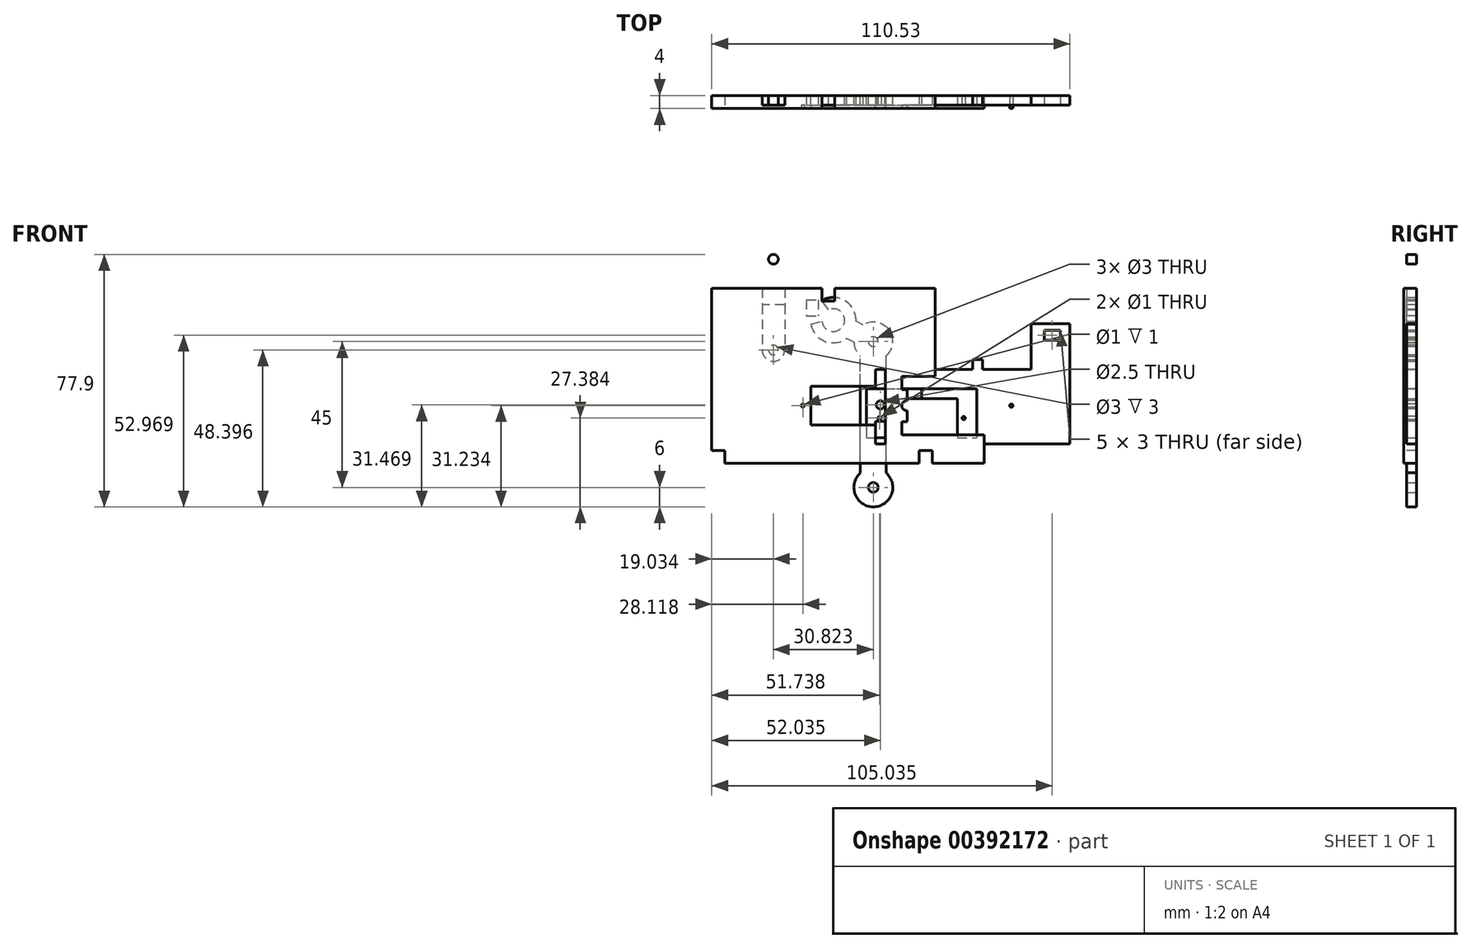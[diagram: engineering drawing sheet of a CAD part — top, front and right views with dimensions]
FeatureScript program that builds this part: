
annotation { "Feature Type Name" : "Feature", "Feature Type Description" : "" }
export const myFeature = defineFeature(function(context is Context, id is Id, definition is map)
    precondition{}
    {
        {
            var Q0;
            Q0=qCreatedBy(makeId("Front.planeOp"),FACE);
            var sketch = newSketch(context, id + "F0", { "sketchPlane" : qUnion([Q0])});
            skLineSegment(sketch, "E0.bottom", {"start": v(-55.1, 26.52) * mm, "end": v(28.9, 26.52) * mm});
            skLineSegment(sketch, "E0.top", {"start": v(-55.1, -27.48) * mm, "end": v(28.9, -27.48) * mm});
            skLineSegment(sketch, "E0.left", {"start": v(-55.1, 26.52) * mm, "end": v(-55.1, -27.48) * mm});
            skLineSegment(sketch, "E0.right", {"start": v(28.9, 26.52) * mm, "end": v(28.9, -27.48) * mm});
            skSolve(sketch);
        }
        {
            var Q0;
            Q0=makeQuery(id+"F0.imprint","IMPRINT",FACE,{"disambiguationData":[TD([[makeQuery(id+"F0.imprint","IMPRINT",EDGE,{"derivedFrom":sQuery(id+"F0.wireOp",EDGE,"E0.bottom")}),-1.0]])]});
            var sketch = newSketch(context, id + "F1", { "sketchPlane" : qUnion([Q0])});
            skSolve(sketch);
        }
        {
            var Q0;
            Q0 = qSketchRegion(id + "F1", true);
            var Q1;
            Q1=makeQuery(id+"F0.imprint","IMPRINT",FACE,{"disambiguationData":[TD([[makeQuery(id+"F0.imprint","IMPRINT",EDGE,{"derivedFrom":sQuery(id+"F0.wireOp",EDGE,"E0.bottom")}),-1.0]])]});
            extrude(context, id + "F2", {"entities" : qUnion([Q0, Q1]), "depth" : 4 * mm});
        }
        {
            var Q0;
            Q0=makeQuery(id+"F2.opExtrude","CAP_FACE",FACE,{"disambiguationData":[OSD([sQuery(id+"F0.wireOp",EDGE,"E0.bottom"),sQuery(id+"F0.wireOp",EDGE,"E0.top"),sQuery(id+"F0.wireOp",EDGE,"E0.left"),sQuery(id+"F0.wireOp",EDGE,"E0.right")])],"isStart":false});
            var sketch = newSketch(context, id + "F3", { "sketchPlane" : qUnion([Q0])});
            skLineSegment(sketch, "E1.bottom", {"start": v(28.9, 26.52) * mm, "end": v(13.9, 26.52) * mm});
            skLineSegment(sketch, "E1.top", {"start": v(28.9, -7.48) * mm, "end": v(13.9, -7.48) * mm});
            skLineSegment(sketch, "E1.left", {"start": v(28.9, 26.52) * mm, "end": v(28.9, -7.48) * mm});
            skLineSegment(sketch, "E1.right", {"start": v(13.9, 26.52) * mm, "end": v(13.9, -7.48) * mm});
            skSolve(sketch);
        }
        {
            var Q0;
            Q0=makeQuery(id+"F3.imprint","IMPRINT",FACE,{"disambiguationData":[TD([[makeQuery(id+"F3.imprint","IMPRINT",EDGE,{"derivedFrom":sQuery(id+"F3.wireOp",EDGE,"E1.bottom")}),-1.0]])]});
            extrude(context, id + "F4", {"entities" : qUnion([Q0]), "operationType" : NewBodyOperationType.REMOVE, "oppositeDirection" : true, "depth" : 5 * mm});
        }
        {
            var Q0;
            Q0=makeQuery(id+"F2.opExtrude","CAP_FACE",FACE,{"disambiguationData":[OSD([sQuery(id+"F0.wireOp",EDGE,"E0.bottom"),sQuery(id+"F0.wireOp",EDGE,"E0.top"),sQuery(id+"F0.wireOp",EDGE,"E0.left"),sQuery(id+"F0.wireOp",EDGE,"E0.right")])],"isStart":false});
            var sketch = newSketch(context, id + "F5", { "sketchPlane" : qUnion([Q0])});
            skLineSegment(sketch, "E2", {"start": v(28.9, -27.48) * mm, "end": v(12.9, -27.48) * mm});
            skLineSegment(sketch, "E3.bottom", {"start": v(12.9, -27.48) * mm, "end": v(8.9, -27.48) * mm});
            skLineSegment(sketch, "E3.top", {"start": v(12.9, -23.48) * mm, "end": v(8.9, -23.48) * mm});
            skLineSegment(sketch, "E3.left", {"start": v(12.9, -27.48) * mm, "end": v(12.9, -23.48) * mm});
            skLineSegment(sketch, "E3.right", {"start": v(8.9, -27.48) * mm, "end": v(8.9, -23.48) * mm});
            skLineSegment(sketch, "E4.bottom", {"start": v(-55.1, -27.48) * mm, "end": v(-51.1, -27.48) * mm});
            skLineSegment(sketch, "E4.top", {"start": v(-55.1, -23.48) * mm, "end": v(-51.1, -23.48) * mm});
            skLineSegment(sketch, "E4.left", {"start": v(-55.1, -27.48) * mm, "end": v(-55.1, -23.48) * mm});
            skLineSegment(sketch, "E4.right", {"start": v(-51.1, -27.48) * mm, "end": v(-51.1, -23.48) * mm});
            skLineSegment(sketch, "E5", {"start": v(13.9, 26.52) * mm, "end": v(-17.1, 26.52) * mm});
            skLineSegment(sketch, "E6.bottom", {"start": v(-17.1, 26.52) * mm, "end": v(-21.1, 26.52) * mm});
            skLineSegment(sketch, "E6.top", {"start": v(-17.1, 22.52) * mm, "end": v(-21.1, 22.52) * mm});
            skLineSegment(sketch, "E6.left", {"start": v(-17.1, 26.52) * mm, "end": v(-17.1, 22.52) * mm});
            skLineSegment(sketch, "E6.right", {"start": v(-21.1, 26.52) * mm, "end": v(-21.1, 22.52) * mm});
            skSolve(sketch);
        }
        {
            var Q0;
            Q0=makeQuery(id+"F5.imprint","IMPRINT",FACE,{"disambiguationData":[TD([[makeQuery(id+"F5.imprint","IMPRINT",EDGE,{"derivedFrom":sQuery(id+"F5.wireOp",EDGE,"E6.bottom")}),-1.0]])]});
            var Q1;
            Q1=makeQuery(id+"F5.imprint","IMPRINT",FACE,{"disambiguationData":[TD([[makeQuery(id+"F5.imprint","IMPRINT",EDGE,{"derivedFrom":sQuery(id+"F5.wireOp",EDGE,"E4.bottom")}),1.0]])]});
            var Q2;
            Q2=makeQuery(id+"F5.imprint","IMPRINT",FACE,{"disambiguationData":[TD([[makeQuery(id+"F5.imprint","IMPRINT",EDGE,{"derivedFrom":sQuery(id+"F5.wireOp",EDGE,"E3.bottom")}),1.0]])]});
            extrude(context, id + "F6", {"entities" : qUnion([Q0, Q1, Q2]), "operationType" : NewBodyOperationType.REMOVE, "oppositeDirection" : true, "depth" : 5 * mm});
        }
        {
            var Q0;
            Q0=qCreatedBy(makeId("Front.planeOp"),FACE);
            var sketch = newSketch(context, id + "F7", { "sketchPlane" : qUnion([Q0])});
            skLineSegment(sketch, "E7.bottom", {"start": v(-30.5, -0.7) * mm, "end": v(40.5, -0.7) * mm});
            skLineSegment(sketch, "E7.top", {"start": v(-30.5, -18.7) * mm, "end": v(40.5, -18.7) * mm});
            skLineSegment(sketch, "E7.left", {"start": v(-30.5, -0.7) * mm, "end": v(-30.5, -18.7) * mm});
            skLineSegment(sketch, "E7.right", {"start": v(40.5, -0.7) * mm, "end": v(40.5, -18.7) * mm});
            skSolve(sketch);
        }
        {
            var Q0;
            Q0=makeQuery(id+"F7.imprint","IMPRINT",FACE,{"disambiguationData":[TD([[makeQuery(id+"F7.imprint","IMPRINT",EDGE,{"derivedFrom":sQuery(id+"F7.wireOp",EDGE,"E7.bottom")}),-1.0]])]});
            extrude(context, id + "F8", {"entities" : qUnion([Q0]), "depth" : 4 * mm});
        }
        {
            var Q0;
            Q0=makeQuery(id+"F8.opExtrude","CAP_FACE",FACE,{"disambiguationData":[OSD([sQuery(id+"F7.wireOp",EDGE,"E7.bottom"),sQuery(id+"F7.wireOp",EDGE,"E7.top"),sQuery(id+"F7.wireOp",EDGE,"E7.left"),sQuery(id+"F7.wireOp",EDGE,"E7.right")])],"isStart":false});
            var sketch = newSketch(context, id + "F9", { "sketchPlane" : qUnion([Q0])});
            skLineSegment(sketch, "E8", {"start": v(-30.5, -9.7) * mm, "end": v(-24.5, -9.7) * mm});
            skLineSegment(sketch, "E9", {"start": v(-15.75, -0.7) * mm, "end": v(-15.75, -3.7) * mm});
            skLineSegment(sketch, "E10", {"start": v(-15.75, -3.7) * mm, "end": v(-24.5, -3.7) * mm});
            skLineSegment(sketch, "E11", {"start": v(-24.5, -3.7) * mm, "end": v(-24.5, -18.7) * mm});
            skLineSegment(sketch, "E12.bottom", {"start": v(-24.5, -3.7) * mm, "end": v(-1.5, -3.7) * mm});
            skLineSegment(sketch, "E12.top", {"start": v(-24.5, -15.7) * mm, "end": v(-1.5, -15.7) * mm});
            skLineSegment(sketch, "E12.left", {"start": v(-24.5, -3.7) * mm, "end": v(-24.5, -15.7) * mm});
            skLineSegment(sketch, "E12.right", {"start": v(-1.5, -3.7) * mm, "end": v(-1.5, -15.7) * mm});
            skLineSegment(sketch, "E13", {"start": v(40.5, -9.7) * mm, "end": v(34.5, -9.7) * mm});
            skPoint(sketch, "E13.endSnap0", {"position": v(40.5, -9.7) * mm});
            skLineSegment(sketch, "E14", {"start": v(34.5, -9.7) * mm, "end": v(34.5, 8.83) * mm});
            skLineSegment(sketch, "E15", {"start": v(27.7, -0.7) * mm, "end": v(27.7, -3.7) * mm});
            skLineSegment(sketch, "E16", {"start": v(27.7, -3.7) * mm, "end": v(34.5, -3.7) * mm});
            skLineSegment(sketch, "E17.bottom", {"start": v(34.5, -3.7) * mm, "end": v(11.5, -3.7) * mm});
            skLineSegment(sketch, "E17.top", {"start": v(34.5, -15.7) * mm, "end": v(11.5, -15.7) * mm});
            skLineSegment(sketch, "E17.left", {"start": v(34.5, -3.7) * mm, "end": v(34.5, -15.7) * mm});
            skLineSegment(sketch, "E17.right", {"start": v(11.5, -3.7) * mm, "end": v(11.5, -15.7) * mm});
            skSolve(sketch);
        }
        {
            var Q0;
            {var subQ4=sQuery(id+"F9.wireOp",EDGE,"E12.top");Q0=makeQuery(id+"F9.imprint","IMPRINT",FACE,{"disambiguationData":[TD([[makeQuery(id+"F9.imprint","IMPRINT",EDGE,{"derivedFrom":subQ4}),1.0]])]});}
            var Q1;
            {var subQ4=sQuery(id+"F9.wireOp",EDGE,"E17.top");Q1=makeQuery(id+"F9.imprint","IMPRINT",FACE,{"disambiguationData":[TD([[makeQuery(id+"F9.imprint","IMPRINT",EDGE,{"derivedFrom":subQ4}),-1.0]])]});}
            extrude(context, id + "F10", {"entities" : qUnion([Q0, Q1]), "operationType" : NewBodyOperationType.REMOVE, "oppositeDirection" : true, "depth" : 5 * mm});
        }
        {
            var Q0;
            Q0=makeQuery(id+"F8.opExtrude","CAP_FACE",FACE,{"disambiguationData":[OSD([sQuery(id+"F7.wireOp",EDGE,"E7.bottom"),sQuery(id+"F7.wireOp",EDGE,"E7.top"),sQuery(id+"F7.wireOp",EDGE,"E7.left"),sQuery(id+"F7.wireOp",EDGE,"E7.right")])],"isStart":false});
            var sketch = newSketch(context, id + "F11", { "sketchPlane" : qUnion([Q0])});
            skLineSegment(sketch, "E18", {"start": v(11.5, -3.7) * mm, "end": v(6.5, -3.7) * mm});
            skPoint(sketch, "E18.endSnap0", {"position": v(5, -0.7) * mm});
            skLineSegment(sketch, "E19", {"start": v(-1.5, -3.7) * mm, "end": v(3.5, -3.7) * mm});
            skLineSegment(sketch, "E20", {"start": v(3.5, -3.7) * mm, "end": v(3.5, 4.46) * mm});
            skPoint(sketch, "E21.firstSnap0", {"position": v(3.5, 0.38) * mm});
            skLineSegment(sketch, "E21.bottom", {"start": v(3.5, -0.7) * mm, "end": v(6.5, -0.7) * mm});
            skLineSegment(sketch, "E21.top", {"start": v(3.5, -4.7) * mm, "end": v(6.5, -4.7) * mm});
            skLineSegment(sketch, "E21.left", {"start": v(3.5, -0.7) * mm, "end": v(3.5, -4.7) * mm});
            skLineSegment(sketch, "E21.right", {"start": v(6.5, -0.7) * mm, "end": v(6.5, -4.7) * mm});
            skLineSegment(sketch, "E22", {"start": v(-7.33, -9.7) * mm, "end": v(23.66, -9.7) * mm});
            skPoint(sketch, "E22.startSnap0", {"position": v(-1.5, -9.7) * mm});
            skLineSegment(sketch, "E23.MirrorCS", {"start": v(3.5, -14.7) * mm, "end": v(6.5, -14.7) * mm});
            skLineSegment(sketch, "E24.MirrorCS", {"start": v(6.5, -18.7) * mm, "end": v(6.5, -14.7) * mm});
            skLineSegment(sketch, "E25.MirrorCS", {"start": v(3.5, -15.7) * mm, "end": v(3.5, -23.85) * mm});
            skLineSegment(sketch, "E26.MirrorCS", {"start": v(3.5, -18.7) * mm, "end": v(3.5, -14.7) * mm});
            skLineSegment(sketch, "E27.MirrorCS", {"start": v(3.5, -18.7) * mm, "end": v(6.5, -18.7) * mm});
            skLineSegment(sketch, "E28.MirrorCS", {"start": v(-1.5, -15.7) * mm, "end": v(3.5, -15.7) * mm});
            skLineSegment(sketch, "E29.MirrorCS", {"start": v(11.5, -15.7) * mm, "end": v(6.5, -15.7) * mm});
            skSolve(sketch);
        }
        {
            var Q0;
            {var subQ3=sQuery(id+"F11.wireOp",EDGE,"E21.bottom");Q0=makeQuery(id+"F11.imprint","IMPRINT",FACE,{"disambiguationData":[TD([[makeQuery(id+"F11.imprint","IMPRINT",EDGE,{"derivedFrom":subQ3}),-1.0]])]});}
            var Q1;
            {var subQ5=sQuery(id+"F11.wireOp",EDGE,"E23.MirrorCS");Q1=makeQuery(id+"F11.imprint","IMPRINT",FACE,{"disambiguationData":[TD([[makeQuery(id+"F11.imprint","IMPRINT",EDGE,{"derivedFrom":subQ5}),-1.0]])]});}
            extrude(context, id + "F12", {"entities" : qUnion([Q0, Q1]), "operationType" : NewBodyOperationType.REMOVE, "oppositeDirection" : true, "depth" : 5 * mm});
        }
        {
            var Q0;
            Q0=makeQuery(id+"F8.opExtrude","CAP_FACE",FACE,{"disambiguationData":[OSD([sQuery(id+"F7.wireOp",EDGE,"E7.bottom"),sQuery(id+"F7.wireOp",EDGE,"E7.top"),sQuery(id+"F7.wireOp",EDGE,"E7.left"),sQuery(id+"F7.wireOp",EDGE,"E7.right")])],"isStart":false});
            var sketch = newSketch(context, id + "F13", { "sketchPlane" : qUnion([Q0])});
            skLineSegment(sketch, "E30", {"start": v(-30.5, -9.7) * mm, "end": v(-27, -9.7) * mm});
            skPoint(sketch, "E30.endSnap0", {"position": v(-24.5, -9.7) * mm});
            skCircle(sketch, "E31", {"center": v(-27, -9.7) * mm, "radius": 0.5 * mm});
            skLineSegment(sketch, "E32", {"start": v(5.16, 3.88) * mm, "end": v(5.16, -32.27) * mm});
            skLineSegment(sketch, "E33.MirrorCS", {"start": v(40.8, -9.7) * mm, "end": v(37.3, -9.7) * mm});
            skCircle(sketch, "E34.MirrorC", {"center": v(37.3, -9.7) * mm, "radius": 0.5 * mm});
            skSolve(sketch);
        }
        {
            var Q0;
            Q0=makeQuery(id+"F13.imprint","IMPRINT",FACE,{"disambiguationData":[TD([[makeQuery(id+"F13.imprint","IMPRINT",EDGE,{"derivedFrom":sQuery(id+"F13.wireOp",EDGE,"E31")}),1.0]])]});
            var Q1;
            Q1=makeQuery(id+"F13.imprint","IMPRINT",FACE,{"disambiguationData":[TD([[makeQuery(id+"F13.imprint","IMPRINT",EDGE,{"derivedFrom":sQuery(id+"F13.wireOp",EDGE,"E34.MirrorC")}),-1.0]])]});
            extrude(context, id + "F14", {"entities" : qUnion([Q0, Q1]), "operationType" : NewBodyOperationType.REMOVE, "oppositeDirection" : true, "depth" : 5 * mm});
        }
        {
            var Q0;
            Q0=makeQuery(id+"F8.opExtrude","CAP_FACE",FACE,{"disambiguationData":[OSD([sQuery(id+"F7.wireOp",EDGE,"E7.bottom"),sQuery(id+"F7.wireOp",EDGE,"E7.top"),sQuery(id+"F7.wireOp",EDGE,"E7.left"),sQuery(id+"F7.wireOp",EDGE,"E7.right")])],"isStart":false});
            var sketch = newSketch(context, id + "F15", { "sketchPlane" : qUnion([Q0])});
            skLineSegment(sketch, "E35", {"start": v(5, -4.7) * mm, "end": v(5, -9.7) * mm});
            skPoint(sketch, "E35.endSnap0", {"position": v(5, -14.7) * mm});
            skCircle(sketch, "E36", {"center": v(5, -9.7) * mm, "radius": 1.5 * mm});
            skLineSegment(sketch, "E37", {"start": v(11.5, -9.7) * mm, "end": v(9.5, -9.7) * mm});
            skCircle(sketch, "E38", {"center": v(9.5, -9.7) * mm, "radius": 0.5 * mm});
            skLineSegment(sketch, "E39", {"start": v(5.2, -0.7) * mm, "end": v(5.2, -24.79) * mm});
            skCircle(sketch, "E40.MirrorC", {"center": v(0.9, -9.7) * mm, "radius": 0.5 * mm});
            skLineSegment(sketch, "E41.MirrorCS", {"start": v(-1.1, -9.7) * mm, "end": v(0.9, -9.7) * mm});
            skSolve(sketch);
        }
        {
            var Q0;
            Q0=makeQuery(id+"F15.imprint","IMPRINT",FACE,{"disambiguationData":[TD([[makeQuery(id+"F15.imprint","IMPRINT",EDGE,{"derivedFrom":sQuery(id+"F15.wireOp",EDGE,"E40.MirrorC")}),-1.0]])]});
            var Q1;
            Q1=makeQuery(id+"F15.imprint","IMPRINT",FACE,{"disambiguationData":[TD([[makeQuery(id+"F15.imprint","IMPRINT",EDGE,{"derivedFrom":sQuery(id+"F15.wireOp",EDGE,"E38")}),1.0]])]});
            var Q2;
            {var subQ0=sQuery(id+"F15.wireOp",EDGE,"E36");var subQ1=makeQuery(id+"F15.imprint","INTERSECT",VERTEX,{"derivedFrom":[sQuery(id+"F15.wireOp",EDGE,"E35"),subQ0]});Q2=makeQuery(id+"F15.imprint","IMPRINT",FACE,{"disambiguationData":[TD([[makeQuery(id+"F15.imprint","IMPRINT",EDGE,{"disambiguationData":[TD([[subQ1,1.0]])],"derivedFrom":subQ0}),1.0]])]});}
            var Q3;
            {var subQ0=sQuery(id+"F15.wireOp",EDGE,"E39");var subQ1=sQuery(id+"F15.wireOp",EDGE,"E36");var subQ2=makeQuery(id+"F15.imprint","INTERSECT",VERTEX,{"disambiguationData":[OD(0.0)],"derivedFrom":[subQ1,subQ0]});Q3=makeQuery(id+"F15.imprint","IMPRINT",FACE,{"disambiguationData":[TD([[makeQuery(id+"F15.imprint","IMPRINT",EDGE,{"disambiguationData":[TD([[subQ2,1.0]])],"derivedFrom":subQ1}),1.0]])]});}
            extrude(context, id + "F16", {"entities" : qUnion([Q0, Q1, Q2, Q3]), "operationType" : NewBodyOperationType.REMOVE, "oppositeDirection" : true, "depth" : 5 * mm});
        }
        {
            var Q0;
            Q0=qCreatedBy(makeId("Front.planeOp"),FACE);
            var sketch = newSketch(context, id + "F17", { "sketchPlane" : qUnion([Q0])});
            skLineSegment(sketch, "E42.bottom", {"start": v(-40.58, 1.54) * mm, "end": v(55.42, 1.54) * mm});
            skLineSegment(sketch, "E42.top", {"start": v(-40.58, -21.46) * mm, "end": v(55.42, -21.46) * mm});
            skLineSegment(sketch, "E42.left", {"start": v(-40.58, 1.54) * mm, "end": v(-40.58, -21.46) * mm});
            skLineSegment(sketch, "E42.right", {"start": v(55.42, 1.54) * mm, "end": v(55.42, -21.46) * mm});
            skLineSegment(sketch, "E43.bottom", {"start": v(-40.58, 1.54) * mm, "end": v(-37.58, 1.54) * mm});
            skLineSegment(sketch, "E43.top", {"start": v(-40.58, 4.54) * mm, "end": v(-37.58, 4.54) * mm});
            skLineSegment(sketch, "E43.left", {"start": v(-40.58, 1.54) * mm, "end": v(-40.58, 4.54) * mm});
            skLineSegment(sketch, "E43.right", {"start": v(-37.58, 1.54) * mm, "end": v(-37.58, 4.54) * mm});
            skLineSegment(sketch, "E44", {"start": v(-37.58, 1.54) * mm, "end": v(25.42, 1.54) * mm});
            skLineSegment(sketch, "E45.bottom", {"start": v(25.42, 1.54) * mm, "end": v(28.42, 1.54) * mm});
            skLineSegment(sketch, "E45.top", {"start": v(25.42, 4.54) * mm, "end": v(28.42, 4.54) * mm});
            skLineSegment(sketch, "E45.left", {"start": v(25.42, 1.54) * mm, "end": v(25.42, 4.54) * mm});
            skLineSegment(sketch, "E45.right", {"start": v(28.42, 1.54) * mm, "end": v(28.42, 4.54) * mm});
            skLineSegment(sketch, "E46", {"start": v(28.42, 1.54) * mm, "end": v(43.42, 1.54) * mm});
            skLineSegment(sketch, "E47.bottom", {"start": v(55.42, 1.54) * mm, "end": v(43.42, 1.54) * mm});
            skLineSegment(sketch, "E47.top", {"start": v(55.42, 15.54) * mm, "end": v(43.42, 15.54) * mm});
            skLineSegment(sketch, "E47.left", {"start": v(55.42, 1.54) * mm, "end": v(55.42, 15.54) * mm});
            skLineSegment(sketch, "E47.right", {"start": v(43.42, 1.54) * mm, "end": v(43.42, 15.54) * mm});
            skSolve(sketch);
        }
        {
            var Q0;
            Q0 = qSketchRegion(id + "F17", true);
            extrude(context, id + "F18", {"entities" : qUnion([Q0]), "depth" : 3 * mm});
        }
        {
            var Q0;
            Q0=makeQuery(id+"F18.opExtrude","CAP_FACE",FACE,{"disambiguationData":[OSD([sQuery(id+"F17.wireOp",EDGE,"E42.top"),sQuery(id+"F17.wireOp",EDGE,"E42.left"),sQuery(id+"F17.wireOp",EDGE,"E42.right"),sQuery(id+"F17.wireOp",EDGE,"E43.top"),sQuery(id+"F17.wireOp",EDGE,"E43.left"),sQuery(id+"F17.wireOp",EDGE,"E43.right"),sQuery(id+"F17.wireOp",EDGE,"E44"),sQuery(id+"F17.wireOp",EDGE,"E45.top"),sQuery(id+"F17.wireOp",EDGE,"E45.left"),sQuery(id+"F17.wireOp",EDGE,"E45.right"),sQuery(id+"F17.wireOp",EDGE,"E46"),sQuery(id+"F17.wireOp",EDGE,"E47.top"),sQuery(id+"F17.wireOp",EDGE,"E47.left"),sQuery(id+"F17.wireOp",EDGE,"E47.right")])],"isStart":false});
            var sketch = newSketch(context, id + "F19", { "sketchPlane" : qUnion([Q0])});
            skLineSegment(sketch, "E48", {"start": v(55.42, 13.54) * mm, "end": v(52.42, 13.54) * mm});
            skLineSegment(sketch, "E49", {"start": v(52.42, 13.54) * mm, "end": v(52.42, 25.14) * mm});
            skLineSegment(sketch, "E50", {"start": v(49.42, 15.54) * mm, "end": v(49.42, 13.54) * mm});
            skLineSegment(sketch, "E51", {"start": v(49.42, 13.54) * mm, "end": v(58.66, 13.54) * mm});
            skLineSegment(sketch, "E52.bottom", {"start": v(52.42, 13.54) * mm, "end": v(47.42, 13.54) * mm});
            skLineSegment(sketch, "E52.top", {"start": v(52.42, 10.54) * mm, "end": v(47.42, 10.54) * mm});
            skLineSegment(sketch, "E52.left", {"start": v(52.42, 13.54) * mm, "end": v(52.42, 10.54) * mm});
            skLineSegment(sketch, "E52.right", {"start": v(47.42, 13.54) * mm, "end": v(47.42, 10.54) * mm});
            skLineSegment(sketch, "E53", {"start": v(-37.58, 1.54) * mm, "end": v(-4.58, 1.54) * mm});
            skLineSegment(sketch, "E54", {"start": v(-4.58, 1.54) * mm, "end": v(-4.58, -29.43) * mm});
            skLineSegment(sketch, "E55.bottom", {"start": v(-4.58, 1.54) * mm, "end": v(-1.58, 1.54) * mm});
            skLineSegment(sketch, "E55.top", {"start": v(-4.58, -4.46) * mm, "end": v(-1.58, -4.46) * mm});
            skLineSegment(sketch, "E55.left", {"start": v(-4.58, 1.54) * mm, "end": v(-4.58, -4.46) * mm});
            skLineSegment(sketch, "E55.right", {"start": v(-1.58, 1.54) * mm, "end": v(-1.58, -4.46) * mm});
            skLineSegment(sketch, "E56", {"start": v(-3.08, -4.46) * mm, "end": v(-3.08, -9.46) * mm});
            skCircle(sketch, "E57", {"center": v(-3.08, -9.46) * mm, "radius": 1.25 * mm});
            skLineSegment(sketch, "E58", {"start": v(-3.08, -9.46) * mm, "end": v(-22.53, -9.46) * mm});
            skLineSegment(sketch, "E59", {"start": v(-22.53, -9.46) * mm, "end": v(6.43, -9.46) * mm});
            skLineSegment(sketch, "E60.MirrorCS", {"start": v(-4.58, -14.46) * mm, "end": v(-1.58, -14.46) * mm});
            skLineSegment(sketch, "E61.MirrorCS", {"start": v(-1.58, -20.46) * mm, "end": v(-1.58, -14.46) * mm});
            skLineSegment(sketch, "E62.MirrorCS", {"start": v(-4.58, -20.46) * mm, "end": v(-4.58, -14.46) * mm});
            skLineSegment(sketch, "E63.MirrorCS", {"start": v(-4.58, -20.46) * mm, "end": v(-1.58, -20.46) * mm});
            skLineSegment(sketch, "E64", {"start": v(-4.58, -20.46) * mm, "end": v(-4.58, -24.64) * mm});
            skLineSegment(sketch, "E65", {"start": v(-4.58, -24.64) * mm, "end": v(5.23, -24.64) * mm});
            skLineSegment(sketch, "E66", {"start": v(-1.58, -20.46) * mm, "end": v(-1.58, -28.18) * mm});
            skSolve(sketch);
        }
        {
            var Q0;
            Q0=makeQuery(id+"F19.imprint","IMPRINT",FACE,{"disambiguationData":[TD([[makeQuery(id+"F19.imprint","IMPRINT",EDGE,{"derivedFrom":sQuery(id+"F19.wireOp",EDGE,"E55.bottom")}),-1.0]])]});
            var Q1;
            {var subQ0=sQuery(id+"F19.wireOp",EDGE,"E59");var subQ1=sQuery(id+"F19.wireOp",EDGE,"E57");var subQ2=makeQuery(id+"F19.imprint","INTERSECT",VERTEX,{"disambiguationData":[OD(0.0)],"derivedFrom":[subQ1,subQ0]});Q1=makeQuery(id+"F19.imprint","IMPRINT",FACE,{"disambiguationData":[TD([[makeQuery(id+"F19.imprint","IMPRINT",EDGE,{"disambiguationData":[TD([[subQ2,1.0]])],"derivedFrom":subQ1}),1.0]])]});}
            var Q2;
            {var subQ0=sQuery(id+"F19.wireOp",EDGE,"E59");var subQ1=sQuery(id+"F19.wireOp",EDGE,"E56");var subQ2=makeQuery(id+"F19.imprint","INTERSECT",VERTEX,{"derivedFrom":[subQ1,subQ0]});Q2=makeQuery(id+"F19.imprint","IMPRINT",FACE,{"disambiguationData":[TD([[makeQuery(id+"F19.imprint","IMPRINT",EDGE,{"disambiguationData":[TD([[subQ2,1.0]])],"derivedFrom":subQ1}),-1.0]])]});}
            var Q3;
            {var subQ0=sQuery(id+"F19.wireOp",EDGE,"E59");var subQ1=sQuery(id+"F19.wireOp",EDGE,"E56");var subQ2=makeQuery(id+"F19.imprint","INTERSECT",VERTEX,{"derivedFrom":[subQ1,subQ0]});Q3=makeQuery(id+"F19.imprint","IMPRINT",FACE,{"disambiguationData":[TD([[makeQuery(id+"F19.imprint","IMPRINT",EDGE,{"disambiguationData":[TD([[subQ2,1.0]])],"derivedFrom":subQ1}),1.0]])]});}
            var Q4;
            Q4=makeQuery(id+"F19.imprint","IMPRINT",FACE,{"disambiguationData":[TD([[makeQuery(id+"F19.imprint","IMPRINT",EDGE,{"derivedFrom":sQuery(id+"F19.wireOp",EDGE,"E60.MirrorCS")}),-1.0]])]});
            var Q5;
            {var subQ0=sQuery(id+"F19.wireOp",EDGE,"E63.MirrorCS");Q5=makeQuery(id+"F19.imprint","IMPRINT",FACE,{"disambiguationData":[TD([[makeQuery(id+"F19.imprint","IMPRINT",EDGE,{"derivedFrom":subQ0}),-1.0]])]});}
            var Q6;
            Q6=makeQuery(id+"F19.imprint","IMPRINT",FACE,{"disambiguationData":[TD([[makeQuery(id+"F19.imprint","IMPRINT",EDGE,{"derivedFrom":sQuery(id+"F19.wireOp",EDGE,"E52.top")}),-1.0]])]});
            extrude(context, id + "F20", {"entities" : qUnion([Q0, Q1, Q2, Q3, Q4, Q5, Q6]), "operationType" : NewBodyOperationType.ADD, "depth" : 5 * mm});
        }
        {
            var Q0;
            Q0=makeQuery(id+"F20.opExtrude","CAP_FACE",FACE,{"disambiguationData":[OSD([sQuery(id+"F19.wireOp",EDGE,"E55.bottom"),sQuery(id+"F19.wireOp",EDGE,"E55.top"),sQuery(id+"F19.wireOp",EDGE,"E55.left"),sQuery(id+"F19.wireOp",EDGE,"E55.right")])],"isStart":false});
            var Q1;
            Q1=makeQuery(id+"F20.opExtrude","CAP_FACE",FACE,{"disambiguationData":[OSD([sQuery(id+"F17.wireOp",EDGE,"E42.top"),sQuery(id+"F19.wireOp",EDGE,"E60.MirrorCS"),sQuery(id+"F19.wireOp",EDGE,"E61.MirrorCS"),sQuery(id+"F19.wireOp",EDGE,"E62.MirrorCS"),sQuery(id+"F19.wireOp",EDGE,"E64"),sQuery(id+"F19.wireOp",EDGE,"E66")])],"isStart":false});
            var Q2;
            Q2=makeQuery(id+"F20.opExtrude","CAP_FACE",FACE,{"disambiguationData":[OSD([sQuery(id+"F19.wireOp",EDGE,"E57")])],"isStart":false});
            var Q3;
            Q3=makeQuery(id+"F20.opExtrude","CAP_FACE",FACE,{"disambiguationData":[OSD([sQuery(id+"F19.wireOp",EDGE,"E52.bottom"),sQuery(id+"F19.wireOp",EDGE,"E52.top"),sQuery(id+"F19.wireOp",EDGE,"E52.left"),sQuery(id+"F19.wireOp",EDGE,"E52.right")])],"isStart":false});
            extrude(context, id + "F21", {"entities" : qUnion([Q0, Q1, Q2, Q3]), "operationType" : NewBodyOperationType.REMOVE, "oppositeDirection" : true, "depth" : 25 * mm});
        }
        {
            var Q0;
            Q0=qCreatedBy(makeId("Front.planeOp"),FACE);
            var sketch = newSketch(context, id + "F22", { "sketchPlane" : qUnion([Q0])});
            skLineSegment(sketch, "E67.bottom", {"start": v(-39.58, 38.97) * mm, "end": v(-32.58, 38.97) * mm});
            skLineSegment(sketch, "E67.top", {"start": v(-39.58, 3.97) * mm, "end": v(-32.58, 3.97) * mm});
            skLineSegment(sketch, "E67.left", {"start": v(-39.58, 38.97) * mm, "end": v(-39.58, 3.97) * mm});
            skLineSegment(sketch, "E67.right", {"start": v(-32.58, 38.97) * mm, "end": v(-32.58, 3.97) * mm});
            skSolve(sketch);
        }
        {
            var Q0;
            Q0 = qSketchRegion(id + "F22", true);
            extrude(context, id + "F23", {"entities" : qUnion([Q0]), "depth" : 3 * mm});
        }
        {
            var Q0;
            Q0=makeQuery(id+"F23.opExtrude","SWEPT_EDGE",EDGE,{"disambiguationData":[OSD([sQuery(id+"F22.wireOp",EDGE,"E67.bottom"),sQuery(id+"F22.wireOp",EDGE,"E67.left")])]});
            var Q1;
            Q1=makeQuery(id+"F23.opExtrude","SWEPT_EDGE",EDGE,{"disambiguationData":[OSD([sQuery(id+"F22.wireOp",EDGE,"E67.top"),sQuery(id+"F22.wireOp",EDGE,"E67.left")])]});
            var Q2;
            Q2=makeQuery(id+"F23.opExtrude","SWEPT_EDGE",EDGE,{"disambiguationData":[OSD([sQuery(id+"F22.wireOp",EDGE,"E67.top"),sQuery(id+"F22.wireOp",EDGE,"E67.right")])]});
            var Q3;
            Q3=makeQuery(id+"F23.opExtrude","SWEPT_EDGE",EDGE,{"disambiguationData":[OSD([sQuery(id+"F22.wireOp",EDGE,"E67.bottom"),sQuery(id+"F22.wireOp",EDGE,"E67.right")])]});
            fillet(context, id + "F24", {"entities" : qUnion([Q0, Q1, Q2, Q3]), "radius" : 3.5 * mm, "tangentPropagation" : true, "allowEdgeOverflow" : false});
        }
        {
            var Q0;
            Q0=makeQuery(id+"F23.opExtrude","CAP_FACE",FACE,{"disambiguationData":[OSD([sQuery(id+"F22.wireOp",EDGE,"E67.bottom"),sQuery(id+"F22.wireOp",EDGE,"E67.top"),sQuery(id+"F22.wireOp",EDGE,"E67.left"),sQuery(id+"F22.wireOp",EDGE,"E67.right")])],"isStart":false});
            var sketch = newSketch(context, id + "F25", { "sketchPlane" : qUnion([Q0])});
            skLineSegment(sketch, "E68", {"start": v(-36.08, 3.97) * mm, "end": v(-36.08, 7.47) * mm});
            skCircle(sketch, "E69", {"center": v(-36.08, 7.47) * mm, "radius": 1.5 * mm});
            skLineSegment(sketch, "E70", {"start": v(-32.58, 21.47) * mm, "end": v(-53.57, 21.47) * mm});
            skCircle(sketch, "E71.MirrorC", {"center": v(-36.08, 35.47) * mm, "radius": 1.5 * mm});
            skLineSegment(sketch, "E72.MirrorCS", {"start": v(-36.08, 38.97) * mm, "end": v(-36.08, 35.47) * mm});
            skSolve(sketch);
        }
        {
            var Q0;
            Q0=makeQuery(id+"F25.imprint","IMPRINT",FACE,{"disambiguationData":[TD([[makeQuery(id+"F25.imprint","IMPRINT",EDGE,{"derivedFrom":sQuery(id+"F25.wireOp",EDGE,"E71.MirrorC")}),-1.0]])]});
            var Q1;
            Q1=makeQuery(id+"F25.imprint","IMPRINT",FACE,{"disambiguationData":[TD([[makeQuery(id+"F25.imprint","IMPRINT",EDGE,{"derivedFrom":sQuery(id+"F25.wireOp",EDGE,"E69")}),1.0]])]});
            extrude(context, id + "F26", {"entities" : qUnion([Q0, Q1]), "operationType" : NewBodyOperationType.REMOVE, "oppositeDirection" : true, "depth" : 25 * mm});
        }
        {
            var Q0;
            Q0=qCreatedBy(makeId("Front.planeOp"),FACE);
            var sketch = newSketch(context, id + "F27", { "sketchPlane" : qUnion([Q0])});
            skLineSegment(sketch, "E73.bottom", {"start": v(-7.37, -4.55) * mm, "end": v(26.63, -4.55) * mm});
            skLineSegment(sketch, "E73.top", {"start": v(-7.37, -19.55) * mm, "end": v(26.63, -19.55) * mm});
            skLineSegment(sketch, "E73.left", {"start": v(-7.37, -4.55) * mm, "end": v(-7.37, -19.55) * mm});
            skLineSegment(sketch, "E73.right", {"start": v(26.63, -4.55) * mm, "end": v(26.63, -19.55) * mm});
            skLineSegment(sketch, "E74", {"start": v(9.63, -4.55) * mm, "end": v(9.63, -7.55) * mm});
            skPoint(sketch, "E74.endSnap0", {"position": v(9.63, -19.55) * mm});
            skLineSegment(sketch, "E75", {"start": v(-7.37, -12.05) * mm, "end": v(-1.37, -12.05) * mm});
            skLineSegment(sketch, "E76", {"start": v(-10.57, -7.55) * mm, "end": v(45.89, -7.55) * mm});
            skLineSegment(sketch, "E77", {"start": v(-1.37, -2.28) * mm, "end": v(-1.37, -25.62) * mm});
            skLineSegment(sketch, "E78", {"start": v(26.63, -12.05) * mm, "end": v(20.63, -12.05) * mm});
            skLineSegment(sketch, "E79", {"start": v(20.63, -0.97) * mm, "end": v(20.63, -33.24) * mm});
            skSolve(sketch);
        }
        {
            var Q0;
            {var subQ0=sQuery(id+"F27.wireOp",EDGE,"E73.left");var subQ1=sQuery(id+"F27.wireOp",EDGE,"E73.bottom");var subQ2=makeQuery(id+"F27.imprint","INTERSECT",VERTEX,{"derivedFrom":[subQ1,subQ0]});Q0=makeQuery(id+"F27.imprint","IMPRINT",FACE,{"disambiguationData":[TD([[makeQuery(id+"F27.imprint","IMPRINT",EDGE,{"disambiguationData":[TD([[subQ2,-1.0]])],"derivedFrom":subQ1}),-1.0]])]});}
            var Q1;
            {var subQ0=sQuery(id+"F27.wireOp",EDGE,"E75");Q1=makeQuery(id+"F27.imprint","IMPRINT",FACE,{"disambiguationData":[TD([[makeQuery(id+"F27.imprint","IMPRINT",EDGE,{"derivedFrom":subQ0}),1.0]])]});}
            var Q2;
            {var subQ5=sQuery(id+"F27.wireOp",EDGE,"E75");Q2=makeQuery(id+"F27.imprint","IMPRINT",FACE,{"disambiguationData":[TD([[makeQuery(id+"F27.imprint","IMPRINT",EDGE,{"derivedFrom":subQ5}),-1.0]])]});}
            var Q3;
            {var subQ0=sQuery(id+"F27.wireOp",EDGE,"E74");Q3=makeQuery(id+"F27.imprint","IMPRINT",FACE,{"disambiguationData":[TD([[makeQuery(id+"F27.imprint","IMPRINT",EDGE,{"derivedFrom":subQ0}),-1.0]])]});}
            var Q4;
            {var subQ0=sQuery(id+"F27.wireOp",EDGE,"E74");Q4=makeQuery(id+"F27.imprint","IMPRINT",FACE,{"disambiguationData":[TD([[makeQuery(id+"F27.imprint","IMPRINT",EDGE,{"derivedFrom":subQ0}),1.0]])]});}
            var Q5;
            {var subQ0=sQuery(id+"F27.wireOp",EDGE,"E73.right");var subQ1=sQuery(id+"F27.wireOp",EDGE,"E73.bottom");var subQ2=makeQuery(id+"F27.imprint","INTERSECT",VERTEX,{"derivedFrom":[subQ1,subQ0]});Q5=makeQuery(id+"F27.imprint","IMPRINT",FACE,{"disambiguationData":[TD([[makeQuery(id+"F27.imprint","IMPRINT",EDGE,{"disambiguationData":[TD([[subQ2,1.0]])],"derivedFrom":subQ1}),-1.0]])]});}
            var Q6;
            {var subQ0=sQuery(id+"F27.wireOp",EDGE,"E78");Q6=makeQuery(id+"F27.imprint","IMPRINT",FACE,{"disambiguationData":[TD([[makeQuery(id+"F27.imprint","IMPRINT",EDGE,{"derivedFrom":subQ0}),-1.0]])]});}
            var Q7;
            {var subQ5=sQuery(id+"F27.wireOp",EDGE,"E78");Q7=makeQuery(id+"F27.imprint","IMPRINT",FACE,{"disambiguationData":[TD([[makeQuery(id+"F27.imprint","IMPRINT",EDGE,{"derivedFrom":subQ5}),1.0]])]});}
            extrude(context, id + "F28", {"entities" : qUnion([Q0, Q1, Q2, Q3, Q4, Q5, Q6, Q7]), "depth" : 3 * mm});
        }
        {
            var Q0;
            Q0=makeQuery(id+"F28.opExtrude","CAP_FACE",FACE,{"disambiguationData":[OSD([sQuery(id+"F27.wireOp",EDGE,"E73.bottom"),sQuery(id+"F27.wireOp",EDGE,"E73.top"),sQuery(id+"F27.wireOp",EDGE,"E73.left"),sQuery(id+"F27.wireOp",EDGE,"E73.right"),sQuery(id+"F27.wireOp",EDGE,"E76"),sQuery(id+"F27.wireOp",EDGE,"E77"),sQuery(id+"F27.wireOp",EDGE,"E79")])],"isStart":false});
            var sketch = newSketch(context, id + "F29", { "sketchPlane" : qUnion([Q0])});
            skLineSegment(sketch, "E80", {"start": v(-4.37, -19.55) * mm, "end": v(-4.37, -13.55) * mm});
            skLineSegment(sketch, "E81", {"start": v(-1.37, -13.55) * mm, "end": v(-3.37, -13.55) * mm});
            skCircle(sketch, "E82", {"center": v(-3.37, -13.55) * mm, "radius": 0.5 * mm});
            skLineSegment(sketch, "E83", {"start": v(9.63, -3.65) * mm, "end": v(9.63, -25.63) * mm});
            skPoint(sketch, "E83.startSnap0", {"position": v(9.63, -4.55) * mm});
            skPoint(sketch, "E83.endSnap0", {"position": v(9.63, -7.55) * mm});
            skLineSegment(sketch, "E84.MirrorCS", {"start": v(9.63, -23.44) * mm, "end": v(9.63, -1.46) * mm});
            skCircle(sketch, "E85.MirrorC", {"center": v(22.63, -13.55) * mm, "radius": 0.5 * mm});
            skSolve(sketch);
        }
        {
            var Q0;
            Q0=makeQuery(id+"F29.imprint","IMPRINT",FACE,{"disambiguationData":[TD([[makeQuery(id+"F29.imprint","IMPRINT",EDGE,{"derivedFrom":sQuery(id+"F29.wireOp",EDGE,"E82")}),1.0]])]});
            var Q1;
            Q1=makeQuery(id+"F29.imprint","IMPRINT",FACE,{"disambiguationData":[TD([[makeQuery(id+"F29.imprint","IMPRINT",EDGE,{"derivedFrom":sQuery(id+"F29.wireOp",EDGE,"E85.MirrorC")}),-1.0]])]});
            extrude(context, id + "F30", {"entities" : qUnion([Q0, Q1]), "operationType" : NewBodyOperationType.REMOVE, "oppositeDirection" : true, "depth" : 25 * mm});
        }
        {
            var Q0;
            Q0=qCreatedBy(makeId("Front.planeOp"),FACE);
            var sketch = newSketch(context, id + "F31", { "sketchPlane" : qUnion([Q0])});
            skCircle(sketch, "E86", {"center": v(-5.25, 10.07) * mm, "radius": 6 * mm});
            skLineSegment(sketch, "E87", {"start": v(-5.25, 10.07) * mm, "end": v(-5.25, -34.93) * mm});
            skCircle(sketch, "E88", {"center": v(-5.25, -34.93) * mm, "radius": 6 * mm});
            skLineSegment(sketch, "E89", {"start": v(-5.25, -12.43) * mm, "end": v(-1.25, -12.43) * mm});
            skPoint(sketch, "E89.endSnap0", {"position": v(-5.25, -12.43) * mm});
            skLineSegment(sketch, "E90", {"start": v(-1.25, -12.43) * mm, "end": v(-1.25, -30.46) * mm});
            skLineSegment(sketch, "E91", {"start": v(-1.25, -12.43) * mm, "end": v(-1.25, 5.6) * mm});
            skLineSegment(sketch, "E92", {"start": v(-5.25, -12.43) * mm, "end": v(-9.25, -12.43) * mm});
            skLineSegment(sketch, "E93", {"start": v(-9.25, -12.43) * mm, "end": v(-9.25, -30.46) * mm});
            skLineSegment(sketch, "E94", {"start": v(-9.25, -30.46) * mm, "end": v(-9.25, -12.43) * mm});
            skLineSegment(sketch, "E95", {"start": v(-9.25, -12.43) * mm, "end": v(-9.25, 5.6) * mm});
            skLineSegment(sketch, "E96", {"start": v(0.75, 10.15) * mm, "end": v(-3.25, 10.15) * mm});
            skCircle(sketch, "E97", {"center": v(-5.25, 10.07) * mm, "radius": 1.5 * mm});
            skCircle(sketch, "E98", {"center": v(-5.25, -34.93) * mm, "radius": 1.5 * mm});
            skLineSegment(sketch, "E99", {"start": v(-5.25, 10.07) * mm, "end": v(-17.6, 16.68) * mm});
            skArc(sketch, "E100", {"start": v(-24.48, 15.42) * mm, "mid": v(-11.24, 13.75) * mm, "end": v(-21.1, 22.75) * mm});
            skPoint(sketch, "E101.endSnap0", {"position": v(-11.25, 11.58) * mm});
            skLineSegment(sketch, "E102", {"start": v(-11.25, 9.88) * mm, "end": v(-9.83, 12.52) * mm});
            skLineSegment(sketch, "E103", {"start": v(-8.42, 15.17) * mm, "end": v(-12.3, 17.25) * mm});
            skLineSegment(sketch, "E104", {"start": v(-11.25, 9.88) * mm, "end": v(-17.8, 13.4) * mm});
            skArc(sketch, "E105", {"start": v(-21.08, 16.36) * mm, "mid": v(-14.55, 14.95) * mm, "end": v(-19.1, 19.84) * mm});
            skLineSegment(sketch, "E106", {"start": v(-17.6, 16.68) * mm, "end": v(-28.7, 23) * mm});
            skPoint(sketch, "E107.endSnap0", {"position": v(-23.15, 19.84) * mm});
            skLineSegment(sketch, "E108", {"start": v(-23.84, 19.84) * mm, "end": v(-23.6, 20.1) * mm});
            skLineSegment(sketch, "E109", {"start": v(-24.37, 15.45) * mm, "end": v(-21.08, 16.36) * mm});
            skLineSegment(sketch, "E110", {"start": v(-19.1, 19.84) * mm, "end": v(-21.1, 22.75) * mm});
            skLineSegment(sketch, "E111", {"start": v(-21.08, 16.36) * mm, "end": v(-26.28, 14.92) * mm});
            skArc(sketch, "E112.trimOffspring", {"start": v(-23.68, 20.14) * mm, "mid": v(-23.76, 20) * mm, "end": v(-23.84, 19.84) * mm});
            skSolve(sketch);
        }
        {
            var Q0;
            Q0 = qSketchRegion(id + "F31", true);
            extrude(context, id + "F32", {"entities" : qUnion([Q0]), "depth" : 3 * mm});
        }
        {
            var Q0;
            Q0=makeQuery(id+"F32.opExtrude","CAP_FACE",FACE,{"disambiguationData":[OSD([sQuery(id+"F31.wireOp",EDGE,"E86"),sQuery(id+"F31.wireOp",EDGE,"E88"),sQuery(id+"F31.wireOp",EDGE,"E90"),sQuery(id+"F31.wireOp",EDGE,"E91"),sQuery(id+"F31.wireOp",EDGE,"E94"),sQuery(id+"F31.wireOp",EDGE,"E95"),sQuery(id+"F31.wireOp",EDGE,"E97"),sQuery(id+"F31.wireOp",EDGE,"E98"),sQuery(id+"F31.wireOp",EDGE,"E100"),sQuery(id+"F31.wireOp",EDGE,"E103"),sQuery(id+"F31.wireOp",EDGE,"E104"),sQuery(id+"F31.wireOp",EDGE,"E105"),sQuery(id+"F31.wireOp",EDGE,"E110"),sQuery(id+"F31.wireOp",EDGE,"E111")])],"isStart":false});
            var sketch = newSketch(context, id + "F33", { "sketchPlane" : qUnion([Q0])});
            skLineSegment(sketch, "E113.bottom", {"start": v(-25.9, 22.99) * mm, "end": v(-22.27, 22.99) * mm});
            skLineSegment(sketch, "E113.top", {"start": v(-25.9, 17.93) * mm, "end": v(-22.27, 17.93) * mm});
            skLineSegment(sketch, "E113.left", {"start": v(-25.9, 22.99) * mm, "end": v(-25.9, 17.93) * mm});
            skLineSegment(sketch, "E113.right", {"start": v(-22.27, 22.99) * mm, "end": v(-22.27, 17.93) * mm});
            skSolve(sketch);
        }
        {
            var Q0;
            Q0 = qSketchRegion(id + "F33", true);
            extrude(context, id + "F34", {"entities" : qUnion([Q0]), "operationType" : NewBodyOperationType.REMOVE, "oppositeDirection" : true, "depth" : 25 * mm});
        }
    });
